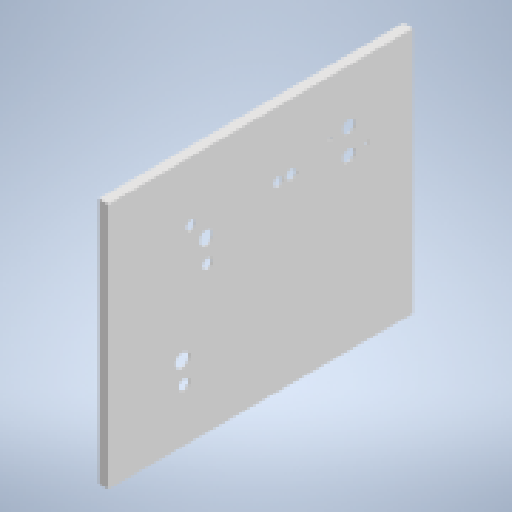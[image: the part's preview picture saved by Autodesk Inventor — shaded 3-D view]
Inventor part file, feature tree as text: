
AUTODESK INVENTOR PART (.ipt)
format: ipt  version: 2023 (Build 270158030, 158C)  size: 187,392 bytes
history: native  units: mm
features: reference x14, other x8, extrude x5, sketch x5
ambient origin geometry x8: Origin, YZ Plane, XZ Plane, XY Plane, X Axis, Y Axis, Z Axis, Center Point
bodies: Solid1 (feature_tree)
feature tree (32):
  extrude  "Extrusion1"  Depth=5.6mm
  extrude  "Extrusion2"  Depth=14.0mm
  extrude  "Extrusion3"  Depth=489.0mm
  extrude  "Extrusion4"  Depth=1.6mm TaperAngle=0.0deg
  extrude  "Extrusion5"  Depth=1.6mm TaperAngle=0.0deg
  sketch  "Sketch1"  dims[d1=5.6mm d2=5.0mm]
  reference  "Reference1"
  sketch  "Sketch2"  dims[d3=10.0mm d4=0.0mm d5=14.0mm]
  reference  "Reference2"
  sketch  "Sketch3"  dims[d6=489.0mm d7=3.0mm]
  sketch  "Sketch4"  dims[d8=3.0mm d9=1.6mm d10=0.0mm]
  sketch  "Sketch5"  dims[d11=396.0mm d12=1.6mm d13=0.0mm d14=1.6mm d15=1.6mm d16=1.6mm d17=1.6mm d18=0.0mm d19=100.0mm d20=0.0mm]
  reference  "Reference3"
  reference  "Reference4"
  reference  "Reference5"
  reference  "Reference6"
  reference  "Reference7"
  reference  "Reference8"
  reference  "Reference9"
  reference  "Reference10"
  reference  "Reference11"
  reference  "Reference12"
  reference  "Reference13"
  reference  "Reference14"
  other  "<userpath>\Documents\0004-inventor\Inventor_Projects\electronics-enclosure\enclosure.iam"
  other  "enclosure.iam"
  other  "enclosure-box:1"
  other  "on-air-control-layout-2:1"
  other  "mode-control-layout:1"
  other  "Part7:4"
  other  "float-indicators:1"
  other  "stop-button:1"
